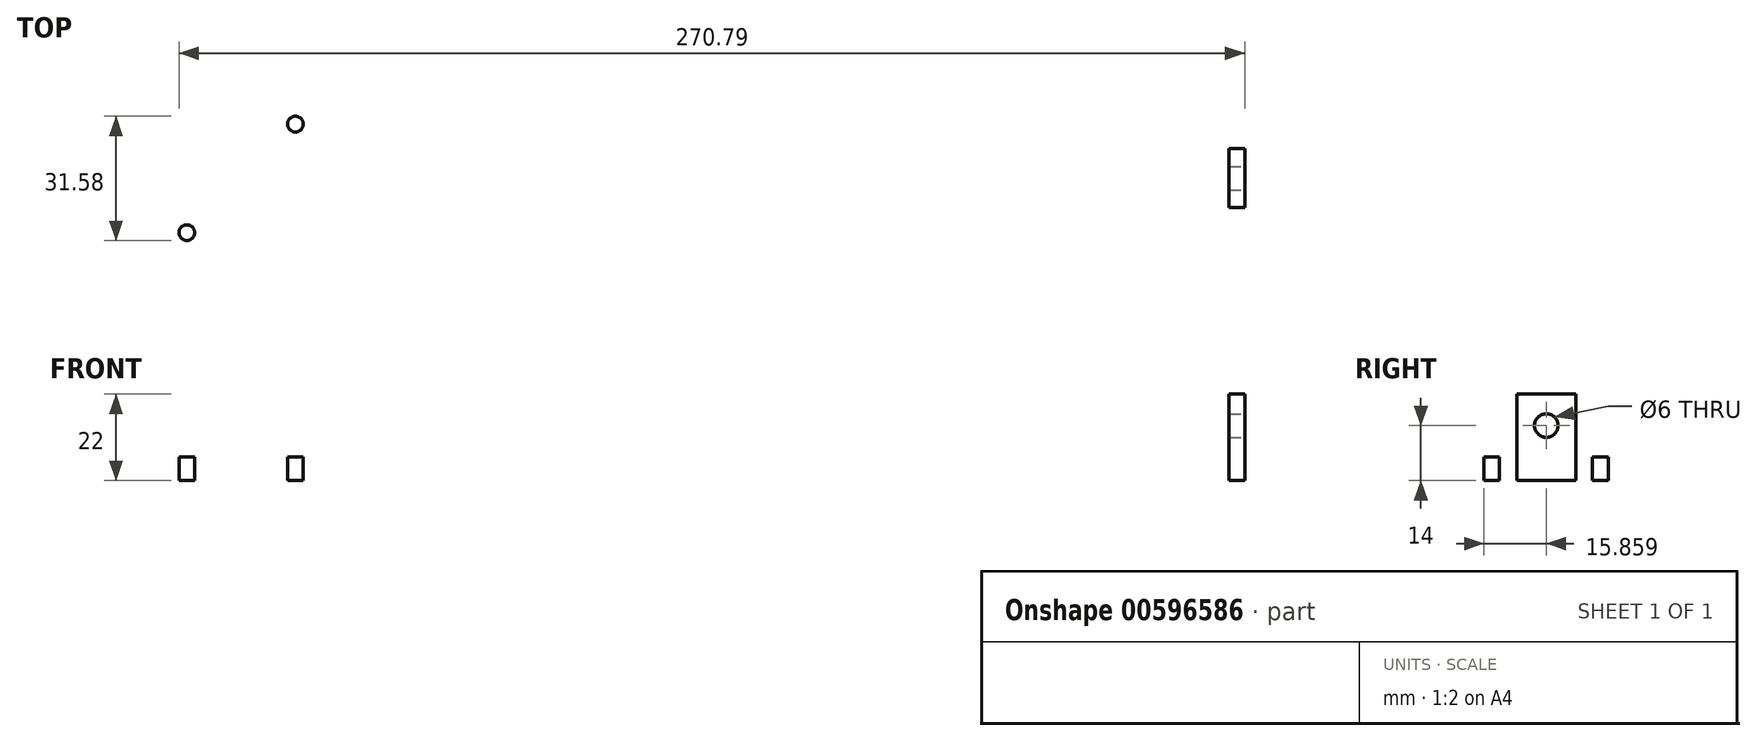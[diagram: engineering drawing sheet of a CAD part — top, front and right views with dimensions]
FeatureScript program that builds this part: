
annotation { "Feature Type Name" : "Feature", "Feature Type Description" : "" }
export const myFeature = defineFeature(function(context is Context, id is Id, definition is map)
    precondition{}
    {
        {
            var Q0;
            Q0=qCreatedBy(makeId("Top.planeOp"),FACE);
            var sketch = newSketch(context, id + "F0", { "sketchPlane" : qUnion([Q0])});
            skLineSegment(sketch, "E0", {"start": v(136.46, -35) * mm, "end": v(-136.46, -35) * mm});
            skLineSegment(sketch, "E1", {"start": v(75, -35) * mm, "end": v(-75, -35) * mm});
            skCircle(sketch, "E2.MirrorC", {"center": v(40, -82) * mm, "radius": 3.25 * mm});
            skArc(sketch, "E3.MirrorCS", {"start": v(131.86, -59) * mm, "mid": v(138, -64.93) * mm, "end": v(132, -71) * mm});
            skArc(sketch, "E4.MirrorCS", {"start": v(88, -71) * mm, "mid": v(82, -65) * mm, "end": v(88, -59) * mm});
            skCircle(sketch, "E5.MirrorC", {"center": v(-40, -52) * mm, "radius": 3.25 * mm});
            skLineSegment(sketch, "E6.MirrorCS", {"start": v(-75, -105) * mm, "end": v(75, -105) * mm});
            skArc(sketch, "E7.MirrorCS", {"start": v(-110, -105) * mm, "mid": v(-147.42, -79.14) * mm, "end": v(-136.46, -35) * mm});
            skLineSegment(sketch, "E8.MirrorCS", {"start": v(88, -59) * mm, "end": v(131.86, -59) * mm});
            skLineSegment(sketch, "E9.MirrorCS", {"start": v(110, -105) * mm, "end": v(-110, -105) * mm});
            skLineSegment(sketch, "E10.MirrorCS", {"start": v(132, -71) * mm, "end": v(88, -71) * mm});
            skArc(sketch, "E11.MirrorCS", {"start": v(136.46, -35) * mm, "mid": v(147.42, -79.14) * mm, "end": v(110, -105) * mm});
            skCircle(sketch, "E12", {"center": v(-110, -65) * mm, "radius": 16 * mm});
            skSolve(sketch);
        }
        {
            var Q0;
            Q0 = qSketchRegion(id + "F0", true);
            extrude(context, id + "F1", {"entities" : qUnion([Q0]), "depth" : 6 * mm, "offsetDistance" : 25 * mm});
        }
        {
            var Q0;
            Q0=makeQuery(id+"F1.opExtrude","CAP_FACE",FACE,{"disambiguationData":[OSD([sQuery(id+"F0.wireOp",EDGE,"E0"),sQuery(id+"F0.wireOp",EDGE,"E2.MirrorC"),sQuery(id+"F0.wireOp",EDGE,"E3.MirrorCS"),sQuery(id+"F0.wireOp",EDGE,"E4.MirrorCS"),sQuery(id+"F0.wireOp",EDGE,"E5.MirrorC"),sQuery(id+"F0.wireOp",EDGE,"E1"),sQuery(id+"F0.wireOp",EDGE,"E7.MirrorCS"),sQuery(id+"F0.wireOp",EDGE,"E8.MirrorCS"),sQuery(id+"F0.wireOp",EDGE,"E9.MirrorCS"),sQuery(id+"F0.wireOp",EDGE,"E10.MirrorCS"),sQuery(id+"F0.wireOp",EDGE,"E11.MirrorCS"),sQuery(id+"F0.wireOp",EDGE,"8672cbab-02df-4e0b-baa1-7fabd20e4ec112.MirrorC")])],"isStart":false});
            var sketch = newSketch(context, id + "F2", { "sketchPlane" : qUnion([Q0])});
            skLineSegment(sketch, "E13.bottom", {"start": v(141, -57.43) * mm, "end": v(145, -57.43) * mm});
            skLineSegment(sketch, "E13.top", {"start": v(141, -72.43) * mm, "end": v(145, -72.43) * mm});
            skLineSegment(sketch, "E13.left", {"start": v(141, -57.43) * mm, "end": v(141, -72.43) * mm});
            skLineSegment(sketch, "E13.right", {"start": v(145, -57.43) * mm, "end": v(145, -72.43) * mm});
            skSolve(sketch);
        }
        {
            var Q0;
            Q0 = qSketchRegion(id + "F2", true);
            extrude(context, id + "F3", {"entities" : qUnion([Q0]), "operationType" : NewBodyOperationType.ADD, "depth" : 16 * mm, "offsetDistance" : 25 * mm});
        }
        {
            var Q0;
            Q0=makeQuery(id+"F3.opExtrude","SWEPT_FACE",FACE,{"disambiguationData":[OSD([sQuery(id+"F2.wireOp",EDGE,"E13.right")])]});
            var sketch = newSketch(context, id + "F4", { "sketchPlane" : qUnion([Q0])});
            skCircle(sketch, "E14", {"center": v(-64.93, 14) * mm, "radius": 3 * mm});
            skPoint(sketch, "E14.centerSnap0", {"position": v(-64.93, 22) * mm});
            skSolve(sketch);
        }
        {
            var Q0;
            Q0=makeQuery(id+"F4.imprint","IMPRINT",FACE,{"disambiguationData":[TD([[makeQuery(id+"F4.imprint","IMPRINT",EDGE,{"derivedFrom":sQuery(id+"F4.wireOp",EDGE,"E14")}),1.0]])]});
            extrude(context, id + "F5", {"entities" : qUnion([Q0]), "operationType" : NewBodyOperationType.REMOVE, "oppositeDirection" : true, "depth" : 25 * mm, "offsetDistance" : 25 * mm});
        }
        {
            var Q0;
            Q0=makeQuery(id+"F1.opExtrude","CAP_FACE",FACE,{"disambiguationData":[OSD([sQuery(id+"F0.wireOp",EDGE,"E0"),sQuery(id+"F0.wireOp",EDGE,"E2.MirrorC"),sQuery(id+"F0.wireOp",EDGE,"E3.MirrorCS"),sQuery(id+"F0.wireOp",EDGE,"E4.MirrorCS"),sQuery(id+"F0.wireOp",EDGE,"E5.MirrorC"),sQuery(id+"F0.wireOp",EDGE,"E1"),sQuery(id+"F0.wireOp",EDGE,"E7.MirrorCS"),sQuery(id+"F0.wireOp",EDGE,"E8.MirrorCS"),sQuery(id+"F0.wireOp",EDGE,"E9.MirrorCS"),sQuery(id+"F0.wireOp",EDGE,"E10.MirrorCS"),sQuery(id+"F0.wireOp",EDGE,"E11.MirrorCS"),sQuery(id+"F0.wireOp",EDGE,"E12")])],"isStart":false});
            var sketch = newSketch(context, id + "F6", { "sketchPlane" : qUnion([Q0])});
            skCircle(sketch, "E15", {"center": v(-110, -65) * mm, "radius": 19.5 * mm, "construction": true});
            skLineSegment(sketch, "E16", {"start": v(-110, -65) * mm, "end": v(-110, -54.6) * mm, "construction": true});
            skLineSegment(sketch, "E17", {"start": v(-110, -65) * mm, "end": v(-116.77, -65) * mm, "construction": true});
            skLineSegment(sketch, "E18", {"start": v(-110, -65) * mm, "end": v(-123.79, -51.21) * mm, "construction": true});
            skCircle(sketch, "E19", {"center": v(-123.79, -51.21) * mm, "radius": 2 * mm});
            skCircle(sketch, "E20.MirrorC", {"center": v(-96.21, -51.21) * mm, "radius": 2 * mm});
            skCircle(sketch, "E21.MirrorC", {"center": v(-123.79, -78.79) * mm, "radius": 2 * mm});
            skCircle(sketch, "E22.MirrorC", {"center": v(-96.21, -78.79) * mm, "radius": 2 * mm});
            skSolve(sketch);
        }
        {
            var Q0;
            Q0=makeQuery(id+"F6.imprint","IMPRINT",FACE,{"disambiguationData":[TD([[makeQuery(id+"F6.imprint","IMPRINT",EDGE,{"derivedFrom":sQuery(id+"F6.wireOp",EDGE,"E19")}),1.0]])]});
            var Q1;
            Q1=makeQuery(id+"F6.imprint","IMPRINT",FACE,{"disambiguationData":[TD([[makeQuery(id+"F6.imprint","IMPRINT",EDGE,{"derivedFrom":sQuery(id+"F6.wireOp",EDGE,"E20.MirrorC")}),-1.0]])]});
            var Q2;
            Q2=makeQuery(id+"F6.imprint","IMPRINT",FACE,{"disambiguationData":[TD([[makeQuery(id+"F6.imprint","IMPRINT",EDGE,{"derivedFrom":sQuery(id+"F6.wireOp",EDGE,"E22.MirrorC")}),1.0]])]});
            var Q3;
            Q3=makeQuery(id+"F6.imprint","IMPRINT",FACE,{"disambiguationData":[TD([[makeQuery(id+"F6.imprint","IMPRINT",EDGE,{"derivedFrom":sQuery(id+"F6.wireOp",EDGE,"E21.MirrorC")}),-1.0]])]});
            extrude(context, id + "F7", {"entities" : qUnion([Q0, Q1, Q2, Q3]), "operationType" : NewBodyOperationType.REMOVE, "oppositeDirection" : true, "depth" : 25 * mm, "offsetDistance" : 25 * mm});
        }
    });
